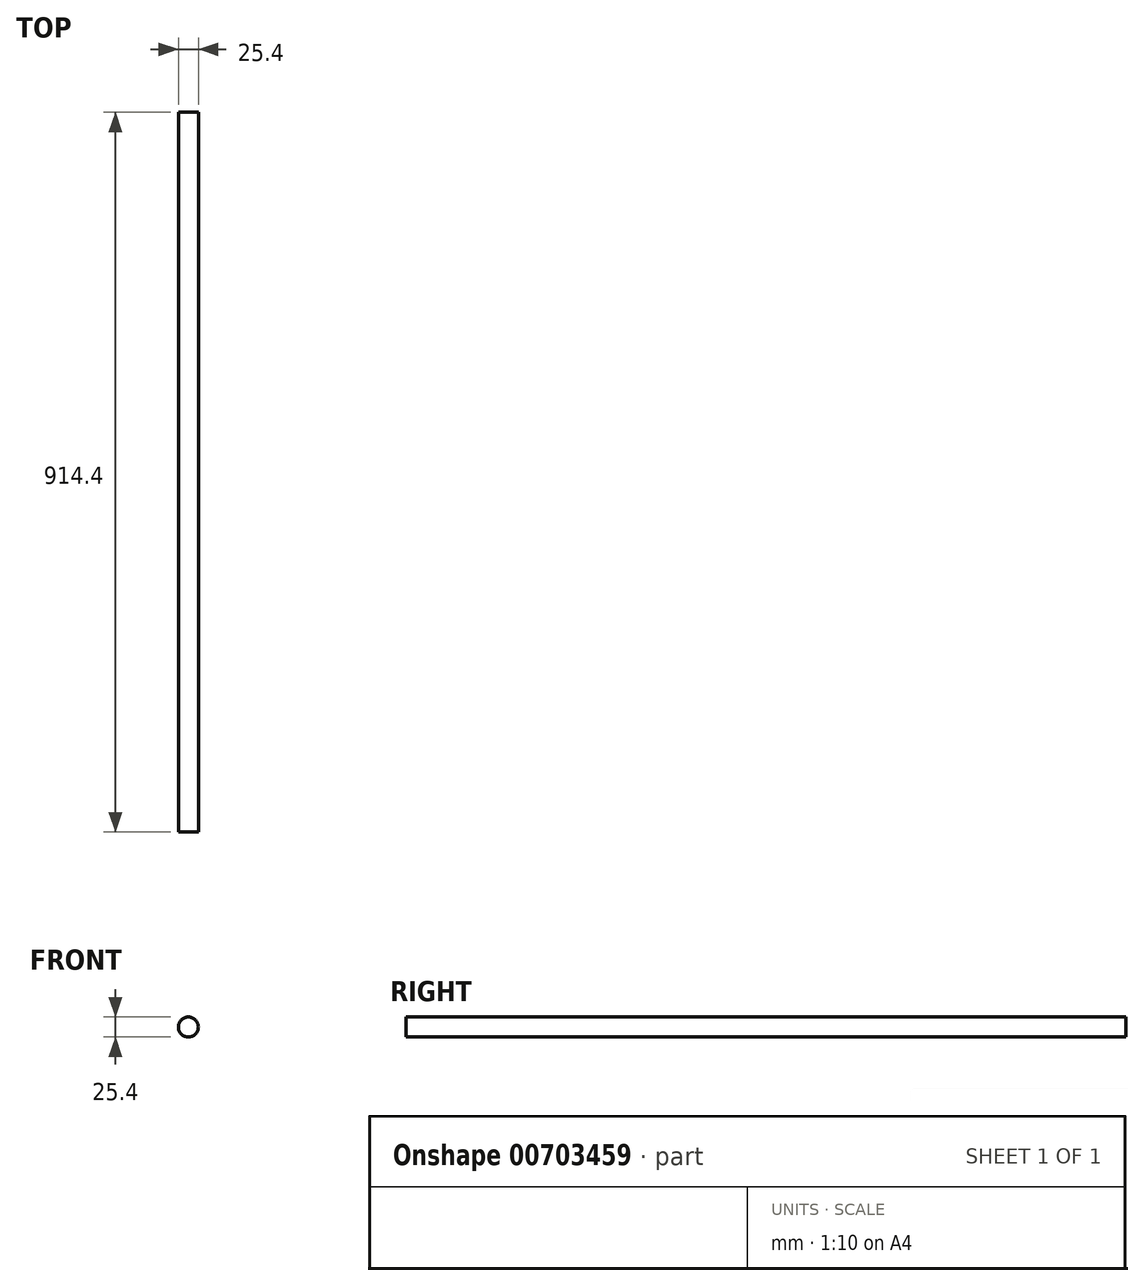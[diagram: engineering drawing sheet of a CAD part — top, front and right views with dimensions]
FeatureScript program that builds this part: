
annotation { "Feature Type Name" : "Feature", "Feature Type Description" : "" }
export const myFeature = defineFeature(function(context is Context, id is Id, definition is map)
    precondition{}
    {
        {
            var Q0;
            Q0=qCreatedBy(makeId("Front.planeOp"),FACE);
            var sketch = newSketch(context, id + "F0", { "sketchPlane" : qUnion([Q0])});
            skCircle(sketch, "E0", {"center": v(0, 0) * mm, "radius": 12.7 * mm});
            skSolve(sketch);
        }
        {
            var Q0;
            Q0=makeQuery(id+"F0.imprint","IMPRINT",FACE,{"disambiguationData":[TD([[makeQuery(id+"F0.imprint","IMPRINT",EDGE,{"derivedFrom":sQuery(id+"F0.wireOp",EDGE,"E0")}),1.0]])]});
            extrude(context, id + "F1", {"entities" : qUnion([Q0]), "depth" : 914.4 * mm, "offsetDistance" : 25.4 * mm});
        }
    });
